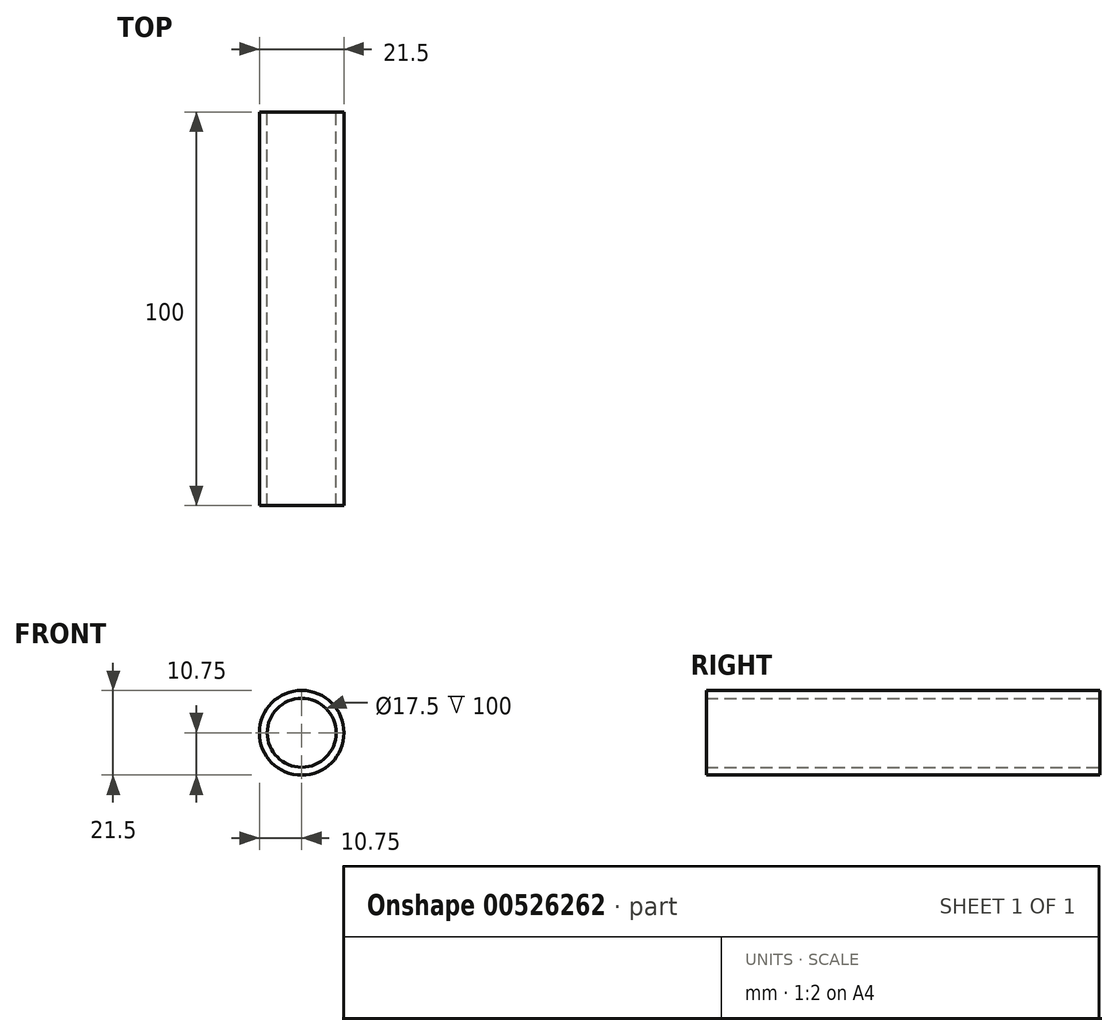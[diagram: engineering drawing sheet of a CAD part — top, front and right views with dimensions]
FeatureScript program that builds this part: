
annotation { "Feature Type Name" : "Feature", "Feature Type Description" : "" }
export const myFeature = defineFeature(function(context is Context, id is Id, definition is map)
    precondition{}
    {
        {
            var Q0;
            Q0=qCreatedBy(makeId("Front.planeOp"),FACE);
            var sketch = newSketch(context, id + "F0", { "sketchPlane" : qUnion([Q0])});
            skCircle(sketch, "E0", {"center": v(0, 0) * mm, "radius": 10.75 * mm});
            skCircle(sketch, "E1", {"center": v(0, 0) * mm, "radius": 8.75 * mm});
            skSolve(sketch);
        }
        {
            var Q0;
            Q0=qSketchRegion(id+"F0",true);
            extrude(context, id + "F1", {"entities" : qUnion([Q0]), "depth" : 100 * mm, "offsetDistance" : 25 * mm});
        }
    });
